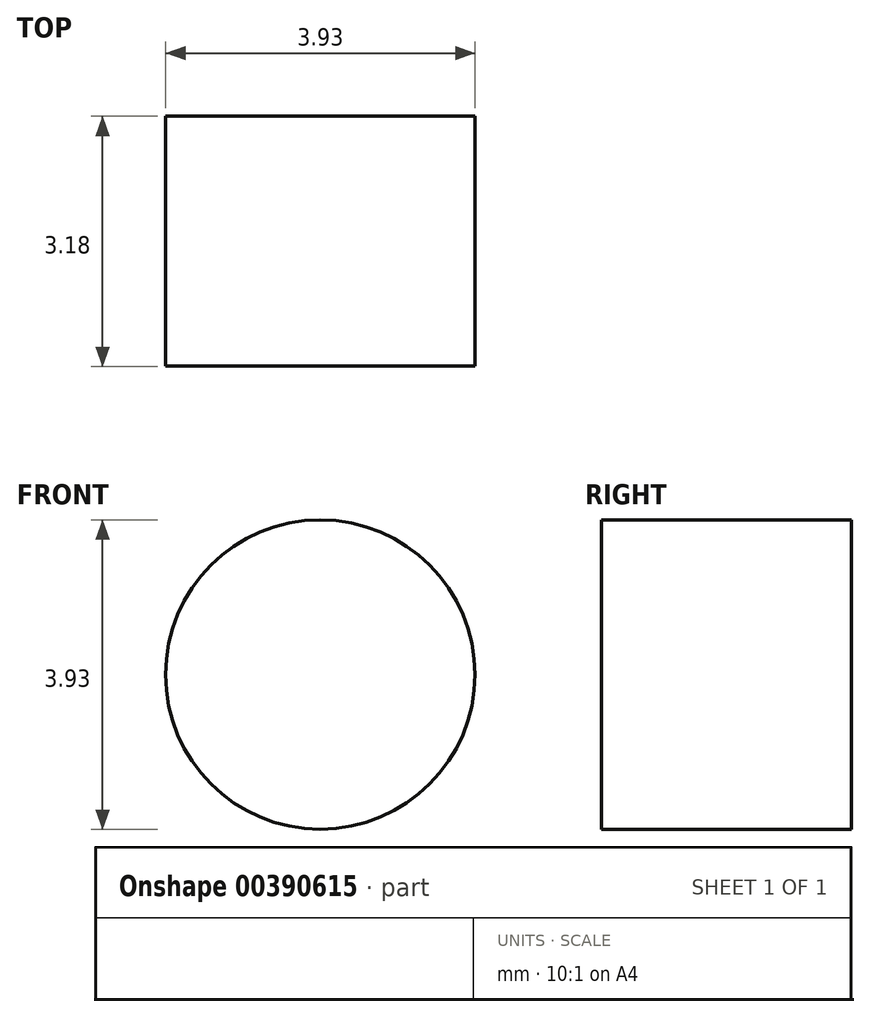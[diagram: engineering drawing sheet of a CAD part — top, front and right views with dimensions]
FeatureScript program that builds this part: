
annotation { "Feature Type Name" : "Feature", "Feature Type Description" : "" }
export const myFeature = defineFeature(function(context is Context, id is Id, definition is map)
    precondition{}
    {
        {
            var Q0;
            Q0=qCreatedBy(makeId("Front.planeOp"),FACE);
            var sketch = newSketch(context, id + "F0", { "sketchPlane" : qUnion([Q0])});
            skCircle(sketch, "E0.MirrorC", {"center": v(28.38, -5.75) * mm, "radius": 1.97 * mm});
            skCircle(sketch, "E1.MirrorC", {"center": v(80.29, -5.75) * mm, "radius": 1.97 * mm});
            skCircle(sketch, "E2.MirrorC", {"center": v(114.28, -5.75) * mm, "radius": 1.97 * mm});
            skCircle(sketch, "E3.MirrorC", {"center": v(165.26, -5.75) * mm, "radius": 1.97 * mm});
            skCircle(sketch, "E4.MirrorC", {"center": v(267.24, -5.75) * mm, "radius": 1.97 * mm});
            skCircle(sketch, "E5.MirrorC", {"center": v(352.21, -5.75) * mm, "radius": 1.97 * mm});
            skCircle(sketch, "E6.MirrorC", {"center": v(394.7, 53.73) * mm, "radius": 1.97 * mm});
            skCircle(sketch, "E7.MirrorC", {"center": v(394.7, 172.7) * mm, "radius": 1.97 * mm});
            skCircle(sketch, "E8.MirrorC", {"center": v(326.72, 172.7) * mm, "radius": 1.97 * mm});
            skCircle(sketch, "E9.MirrorC", {"center": v(326.72, 53.73) * mm, "radius": 1.97 * mm});
            skLineSegment(sketch, "E10", {"start": v(394.7, 172.7) * mm, "end": v(396.67, 172.7) * mm});
            skLineSegment(sketch, "E11", {"start": v(-21.62, -43.85) * mm, "end": v(415.25, -43.85) * mm});
            skLineSegment(sketch, "E12", {"start": v(326.72, 192.7) * mm, "end": v(415.25, 192.7) * mm});
            skPoint(sketch, "E13.orphan", {"position": v(425.25, 172.7) * mm});
            skLineSegment(sketch, "E14", {"start": v(425.25, 182.7) * mm, "end": v(425.25, -33.85) * mm});
            skLineSegment(sketch, "E15", {"start": v(-31.62, 60.45) * mm, "end": v(-31.62, -33.85) * mm});
            skLineSegment(sketch, "E16", {"start": v(-21.62, 70.45) * mm, "end": v(301.71, 70.45) * mm});
            skLineSegment(sketch, "E17", {"start": v(326.72, 192.7) * mm, "end": v(321.71, 192.7) * mm});
            skLineSegment(sketch, "E18", {"start": v(311.71, 182.7) * mm, "end": v(311.71, 80.45) * mm});
            skPoint(sketch, "E19.visualSharp", {"position": v(-31.62, 70.45) * mm});
            skArc(sketch, "E19.filletArc", {"start": v(-21.62, 70.45) * mm, "mid": v(-28.69, 67.52) * mm, "end": v(-31.62, 60.45) * mm});
            skPoint(sketch, "E20.visualSharp", {"position": v(-31.62, -43.85) * mm});
            skArc(sketch, "E20.filletArc", {"start": v(-31.62, -33.85) * mm, "mid": v(-28.69, -40.93) * mm, "end": v(-21.62, -43.85) * mm});
            skPoint(sketch, "E21.visualSharp", {"position": v(425.25, -43.85) * mm});
            skArc(sketch, "E21.filletArc", {"start": v(415.25, -43.85) * mm, "mid": v(422.32, -40.93) * mm, "end": v(425.25, -33.85) * mm});
            skPoint(sketch, "E22.visualSharp", {"position": v(311.71, 70.45) * mm});
            skArc(sketch, "E22.filletArc", {"start": v(301.71, 70.45) * mm, "mid": v(308.78, 73.37) * mm, "end": v(311.71, 80.45) * mm});
            skPoint(sketch, "E23.visualSharp", {"position": v(311.71, 192.7) * mm});
            skArc(sketch, "E23.filletArc", {"start": v(321.71, 192.7) * mm, "mid": v(314.64, 189.77) * mm, "end": v(311.71, 182.7) * mm});
            skPoint(sketch, "E24.visualSharp", {"position": v(425.25, 192.7) * mm});
            skArc(sketch, "E24.filletArc", {"start": v(425.25, 182.7) * mm, "mid": v(422.32, 189.77) * mm, "end": v(415.25, 192.7) * mm});
            skText(sketch, "E25", { "text": "9207", "fontName": "AllertaStencil-Regular.ttf"});
            const initialGuessF0  = {"E25": [-0.01013, 0.0101, 1, 0, 0.0517]};
            skSetInitialGuess(sketch, initialGuessF0);
            skSolve(sketch);
        }
        {
            var Q0;
            Q0=makeQuery(id+"F0.imprint","IMPRINT",FACE,{"disambiguationData":[TD([[makeQuery(id+"F0.imprint","IMPRINT",EDGE,{"derivedFrom":sQuery(id+"F0.wireOp",EDGE,"E0.MirrorC")}),1.0]])]});
            extrude(context, id + "F1", {"entities" : qUnion([Q0]), "depth" : 3.17 * mm});
        }
    });
